# Revit family: Indirect-Water-Heater_Lochinvar_Ltd-SIVS-130_G_E
name_source: partatom
category: Mechanical Equipment
revit_build: Autodesk Revit Architecture 2013 (Build: 20130531_2115(x64)
units: mm (PartAtom-declared; Revit-internal decimal feet)

## types (1)
- Indirect-Water-Heater_Lochinvar_Ltd-SIVS-130_G_E
    1e Maintenance (check-up) = 3 months after installation
    2nd Maintenance (general maintenance) = 12 months after installation
    Assembly Code = D3010
    BIM Content Developer = CAD & Company
    BIM Content Developer URL = http://www.cadcompany.nl
    Cold Water Connection R = 2 1/2"
    Description = Indirect Water Heater
    Destination / Counrty = UK & Ireland
    Diameter (with insulation) = 455 mm
    Diameter (without insulation) = 398 mm  [stored 1.30577 ft]
    Draw-off Capacity @ ΔT = 28°C after 120 min. = 7515.0 L
    Draw-off Capacity @ ΔT = 28°C after 30 min. = 2723.0 L
    Draw-off Capacity @ ΔT = 28°C after 60 min. = 4321.0 L
    Draw-off Capacity @ ΔT = 28°C after 90 min. = 5918.0 L
    Draw-off Capacity @ ΔT = 44°C after 120 min. = 4782.0 L
    Draw-off Capacity @ ΔT = 44°C after 30 min. = 1733.0 L
    Draw-off Capacity @ ΔT = 44°C after 60 min. = 2749.0 L
    Draw-off Capacity @ ΔT = 44°C after 90 min. = 3766.0 L
    Draw-off Capacity @ ΔT = 50°C after 120 min. = 4208.0 L
    Draw-off Capacity @ ΔT = 50°C after 30 min. = 1525.0 L
    Draw-off Capacity @ ΔT = 50°C after 60 min. = 2420.0 L
    Draw-off Capacity @ ΔT = 50°C after 90 min. = 3314.0 L
    Draw-off Capacity @ ΔT = 55°C after 120 min. = 3826.0 L
    Draw-off Capacity @ ΔT = 55°C after 30 min. = 1386.0 L
    Draw-off Capacity @ ΔT = 55°C after 60 min. = 2200.0 L
    Draw-off Capacity @ ΔT = 55°C after 90 min. = 3013.0 L
    Draw-off Capacity @ ΔT = 70°C after 120 min. = 3006.0 L
    Draw-off Capacity @ ΔT = 70°C after 30 min. = 1089.0 L
    Draw-off Capacity @ ΔT = 70°C after 60 min. = 1728.0 L
    Draw-off Capacity @ ΔT = 70°C after 90 min. = 2367.0 L
    Empty Weight = 241.00 kg
    Flow Rate - Volume L/h = 4472
    Heating Up Time @ ΔT = 28°C = 12
    Heating Up Time @ ΔT = 44°C = 19
    Heating Up Time @ ΔT = 50°C = 22
    Heating Up Time @ ΔT = 55°C = 24
    Heating Up Time @ ΔT = 70°C = 30
    Height (with insulation) = 1835 mm  [stored 6.02034 ft]
    Height (without insulation) = 1778 mm  [stored 5.83333 ft]
    Height Cold Water Inlet = 85 mm  [stored 0.278871 ft]
    Height Warm Water Outlet = 1775 mm  [stored 5.82349 ft]
    Hot / Warm Water Connection R = 2 1/2"
    Insulation Thickness = 57 mm  [stored 0.187008 ft]
    Length = 0 mm  [stored 0 ft]
    Maintenance Interval = 12 months
    Manufacturer = Lochinvar Limited
    Manufacturer Number = E 7110
E 7110
E 7110
    Max. Operating Pressure - heat exchanger = 1600000.0 Pa
    Max. Operating Pressure - tank = 1000000.0 Pa
    Max. Temperature - heat exchanger = 110 °C
    Max. Temperature - tank = 95 °C
    Model = SIVS 130 G E
    Nominal Output - heat exchanger = 106000 W
    Operating Weight = 891.00 kg
    Packaging Height = 1930 mm  [stored 6.33202 ft]
    Packaging Length = 870 mm  [stored 2.85433 ft]
    Packaging Width = 870 mm  [stored 2.85433 ft]
    Pressure Loss - heat exchanger 80ºC/60ºC = 10400.0 Pa
    Product Documentation Link = http://www.lochinvar.ltd.uk
    Product Instruction Link = http://www.lochinvar.ltd.uk
    Recovery Rate @ ΔT = 28°C (ltr/hr) = 3194
    Recovery Rate @ ΔT = 44°C (ltr/hr) = 2033
    Recovery Rate @ ΔT = 50°C (ltr/hr) = 1789
    Recovery Rate @ ΔT = 55°C (ltr/hr) = 1626
    Recovery Rate @ ΔT = 70°C (ltr/hr) = 1278
    Serial Number = 8717449269210
    Stand-by Loss = 0 W
    Stand-by Loss - daily (Watt/24H) = 0
    Storage Capacity - heat exchanger = 29.3 m³
    Storage Capacity - tank = 650 m³
    Surface Heat Exchanger = 3.45 m²
    T&P Connection Rp = 1"
    Transport Weight = 251.00 kg
    Type of Packaging = Plastic and Wood
    URL = www.lochinvar.ltd.uk
    Warranty on Parts = 12 months
    Warranty on Tank = 36 months
    Width = 0 mm  [stored 0 ft]
    Workspace = 955 mm  [stored 3.1332 ft]

note: [stored X ft] marks values corroborated as IEEE doubles in the binary element streams (Revit-internal decimal feet)

## geometry (parser evidence)
native form markers: Sweep x14
no freeform markers — native parametric forms only
